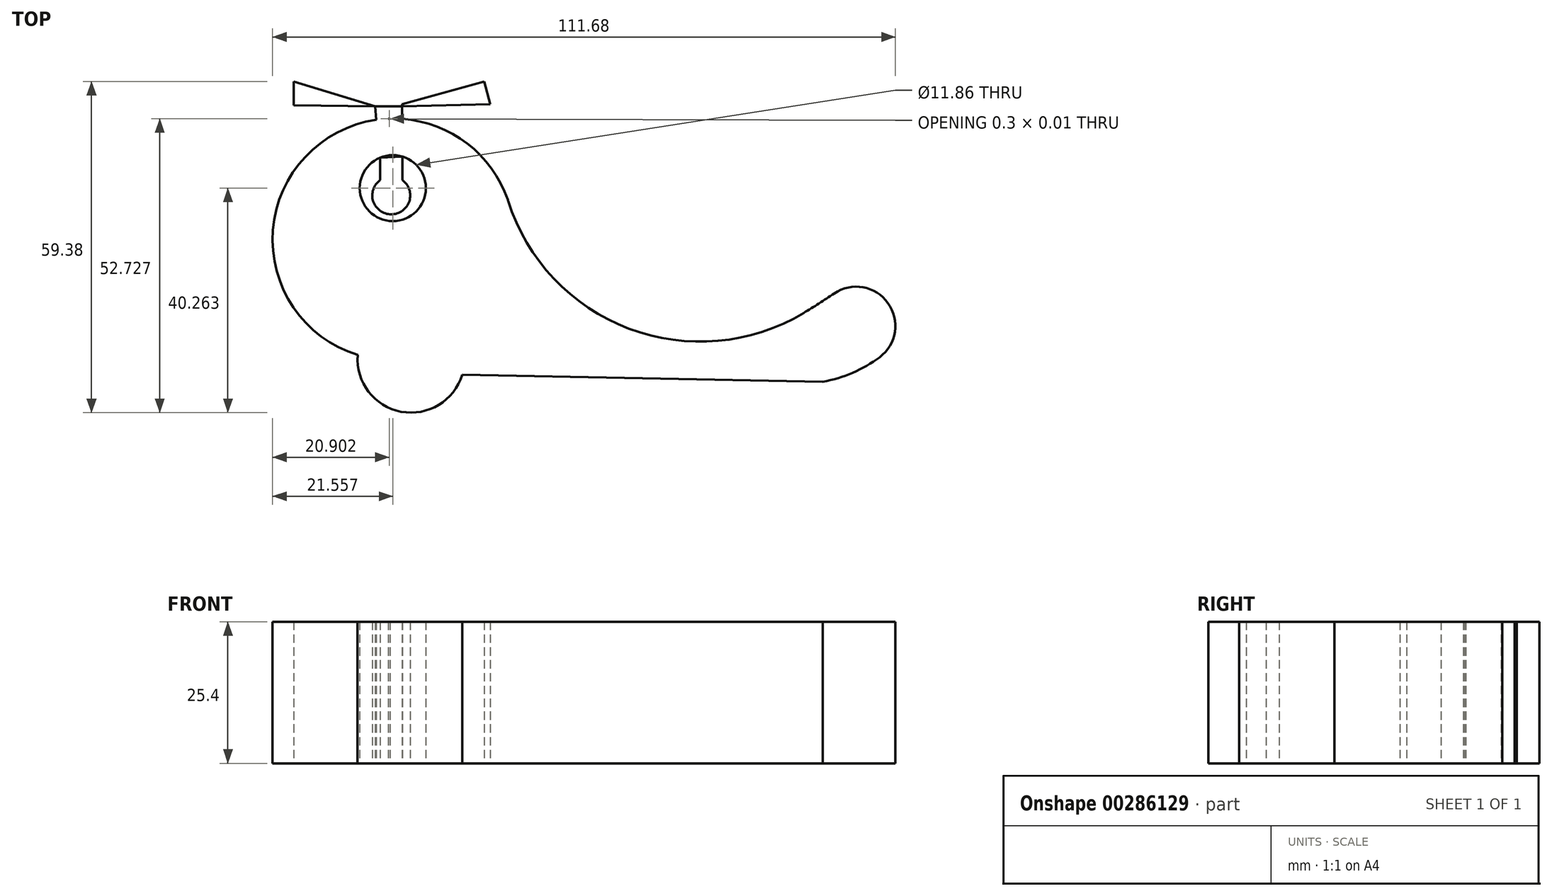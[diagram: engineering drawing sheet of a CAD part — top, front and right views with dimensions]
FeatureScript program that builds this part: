
annotation { "Feature Type Name" : "Feature", "Feature Type Description" : "" }
export const myFeature = defineFeature(function(context is Context, id is Id, definition is map)
    precondition{}
    {
        {
            var Q0;
            Q0=qCreatedBy(makeId("Top.planeOp"),FACE);
            var sketch = newSketch(context, id + "F0", { "sketchPlane" : qUnion([Q0])});
            skArc(sketch, "E0", {"start": v(-11.62, 13.1) * mm, "mid": v(-47.7, 21.03) * mm, "end": v(-38.52, -14.76) * mm});
            skPoint(sketch, "E0.first.point", {"position": v(-11.57, 12.95) * mm});
            skPoint(sketch, "E0.second.point", {"position": v(-53.59, 2.97) * mm});
            skPoint(sketch, "E0.third.point", {"position": v(-28.96, -15.5) * mm});
            skArc(sketch, "E1", {"start": v(-11.54, 12.85) * mm, "mid": v(10.08, -10.02) * mm, "end": v(41.43, -7.22) * mm});
            skArc(sketch, "E2", {"start": v(41.43, -7.22) * mm, "mid": v(44.2, -5.52) * mm, "end": v(46.9, -3.73) * mm});
            skArc(sketch, "E3", {"start": v(46.9, -3.73) * mm, "mid": v(56.57, -5.44) * mm, "end": v(55.08, -15.16) * mm});
            skCircle(sketch, "E4", {"center": v(-28.96, -15.5) * mm, "radius": 9.6 * mm});
            skArc(sketch, "E5.filletArc", {"start": v(-11.54, 12.85) * mm, "mid": v(-11.58, 12.98) * mm, "end": v(-11.62, 13.1) * mm});
            skPoint(sketch, "E6", {"position": v(-33.04, 27.63) * mm});
            skArc(sketch, "E7", {"start": v(55.08, -15.16) * mm, "mid": v(50.23, -17.96) * mm, "end": v(44.85, -19.53) * mm});
            skLineSegment(sketch, "E8", {"start": v(-19.78, -18.3) * mm, "end": v(44.85, -19.53) * mm});
            skArc(sketch, "E9", {"start": v(-30.55, 29.87) * mm, "mid": v(-32.98, 32.5) * mm, "end": v(-35.4, 29.87) * mm});
            skPoint(sketch, "E9.first.point", {"position": v(-34.6, 31.88) * mm});
            skPoint(sketch, "E9.third.point", {"position": v(-33.04, 32.5) * mm});
            skLineSegment(sketch, "E10", {"start": v(-35.4, 29.87) * mm, "end": v(-35.2, 27.43) * mm});
            skLineSegment(sketch, "E11", {"start": v(-30.55, 30.25) * mm, "end": v(-30.55, 27.6) * mm});
            skArc(sketch, "E12.trimOffspring", {"start": v(-33.04, 27.63) * mm, "mid": v(-32.89, 27.63) * mm, "end": v(-32.74, 27.64) * mm});
            skLineSegment(sketch, "E13", {"start": v(-35.4, 29.87) * mm, "end": v(-30.55, 29.87) * mm});
            skLineSegment(sketch, "E14", {"start": v(-30.55, 30.25) * mm, "end": v(-15.86, 34.29) * mm});
            skLineSegment(sketch, "E15", {"start": v(-15.86, 34.29) * mm, "end": v(-14.74, 30.21) * mm});
            skLineSegment(sketch, "E16", {"start": v(-14.74, 30.21) * mm, "end": v(-30.55, 29.87) * mm});
            skLineSegment(sketch, "E17", {"start": v(-35.4, 29.87) * mm, "end": v(-49.99, 34.29) * mm});
            skLineSegment(sketch, "E18", {"start": v(-49.99, 34.29) * mm, "end": v(-49.99, 30.06) * mm});
            skLineSegment(sketch, "E19", {"start": v(-49.99, 30.06) * mm, "end": v(-35.4, 29.87) * mm});
            skCircle(sketch, "E20", {"center": v(-32.23, 15.17) * mm, "radius": 5.93 * mm});
            skPoint(sketch, "E20.first.point", {"position": v(-34.06, 20.81) * mm});
            skPoint(sketch, "E20.second.point", {"position": v(-30.16, 9.62) * mm});
            skPoint(sketch, "E20.third.point", {"position": v(-38.1, 16.03) * mm});
            skCircle(sketch, "E21", {"center": v(-32.51, 13.87) * mm, "radius": 3.4 * mm});
            skPoint(sketch, "E21.first.point", {"position": v(-34.5, 16.63) * mm});
            skPoint(sketch, "E21.second.point", {"position": v(-30.16, 11.41) * mm});
            skPoint(sketch, "E21.third.point", {"position": v(-35.25, 11.85) * mm});
            skLineSegment(sketch, "E22", {"start": v(-34.5, 16.63) * mm, "end": v(-34.5, 20.65) * mm});
            skLineSegment(sketch, "E23", {"start": v(-30.52, 16.63) * mm, "end": v(-30.52, 20.81) * mm});
            skLineSegment(sketch, "E24", {"start": v(-34.5, 20.65) * mm, "end": v(-30.52, 20.81) * mm});
            skSolve(sketch);
        }
        {
            var Q0;
            Q0=makeQuery(id+"F0.imprint","IMPRINT",FACE,{"disambiguationData":[TD([[makeQuery(id+"F0.imprint","IMPRINT",EDGE,{"derivedFrom":sQuery(id+"F0.wireOp",EDGE,"E17")}),1.0]])]});
            var Q1;
            {var subQ3=sQuery(id+"F0.wireOp",EDGE,"E14");Q1=makeQuery(id+"F0.imprint","IMPRINT",FACE,{"disambiguationData":[TD([[makeQuery(id+"F0.imprint","IMPRINT",EDGE,{"derivedFrom":subQ3}),-1.0]])]});}
            var Q2;
            {var subQ0=sQuery(id+"F0.wireOp",EDGE,"E10");Q2=makeQuery(id+"F0.imprint","IMPRINT",FACE,{"disambiguationData":[TD([[makeQuery(id+"F0.imprint","IMPRINT",EDGE,{"derivedFrom":subQ0}),1.0]])]});}
            var Q3;
            {var subQ0=sQuery(id+"F0.wireOp",EDGE,"E22");Q3=makeQuery(id+"F0.imprint","IMPRINT",FACE,{"disambiguationData":[TD([[makeQuery(id+"F0.imprint","IMPRINT",EDGE,{"derivedFrom":subQ0}),-1.0]])]});}
            var Q4;
            {var subQ0=sQuery(id+"F0.wireOp",EDGE,"E21");var subQ1=makeQuery(id+"F0.imprint","INTERSECT",VERTEX,{"derivedFrom":[subQ0,sQuery(id+"F0.wireOp",EDGE,"E22")]});Q4=makeQuery(id+"F0.imprint","IMPRINT",FACE,{"disambiguationData":[TD([[makeQuery(id+"F0.imprint","IMPRINT",EDGE,{"disambiguationData":[TD([[subQ1,1.0]])],"derivedFrom":subQ0}),1.0]])]});}
            var Q5;
            Q5=makeQuery(id+"F0.imprint","IMPRINT",FACE,{"disambiguationData":[TD([[makeQuery(id+"F0.imprint","IMPRINT",EDGE,{"derivedFrom":sQuery(id+"F0.wireOp",EDGE,"E1")}),-1.0]])]});
            var Q6;
            {var subQ0=sQuery(id+"F0.wireOp",EDGE,"E4");var subQ1=makeQuery(id+"F0.imprint","INTERSECT",VERTEX,{"derivedFrom":[sQuery(id+"F0.wireOp",EDGE,"E0"),subQ0]});Q6=makeQuery(id+"F0.imprint","IMPRINT",FACE,{"disambiguationData":[TD([[makeQuery(id+"F0.imprint","IMPRINT",EDGE,{"disambiguationData":[TD([[subQ1,-1.0]])],"derivedFrom":subQ0}),1.0]])]});}
            extrude(context, id + "F1", {"entities" : qUnion([Q0, Q1, Q2, Q3, Q4, Q5, Q6]), "endBound" : BoundingType.SYMMETRIC, "depth" : 25.4 * mm});
        }
    });
